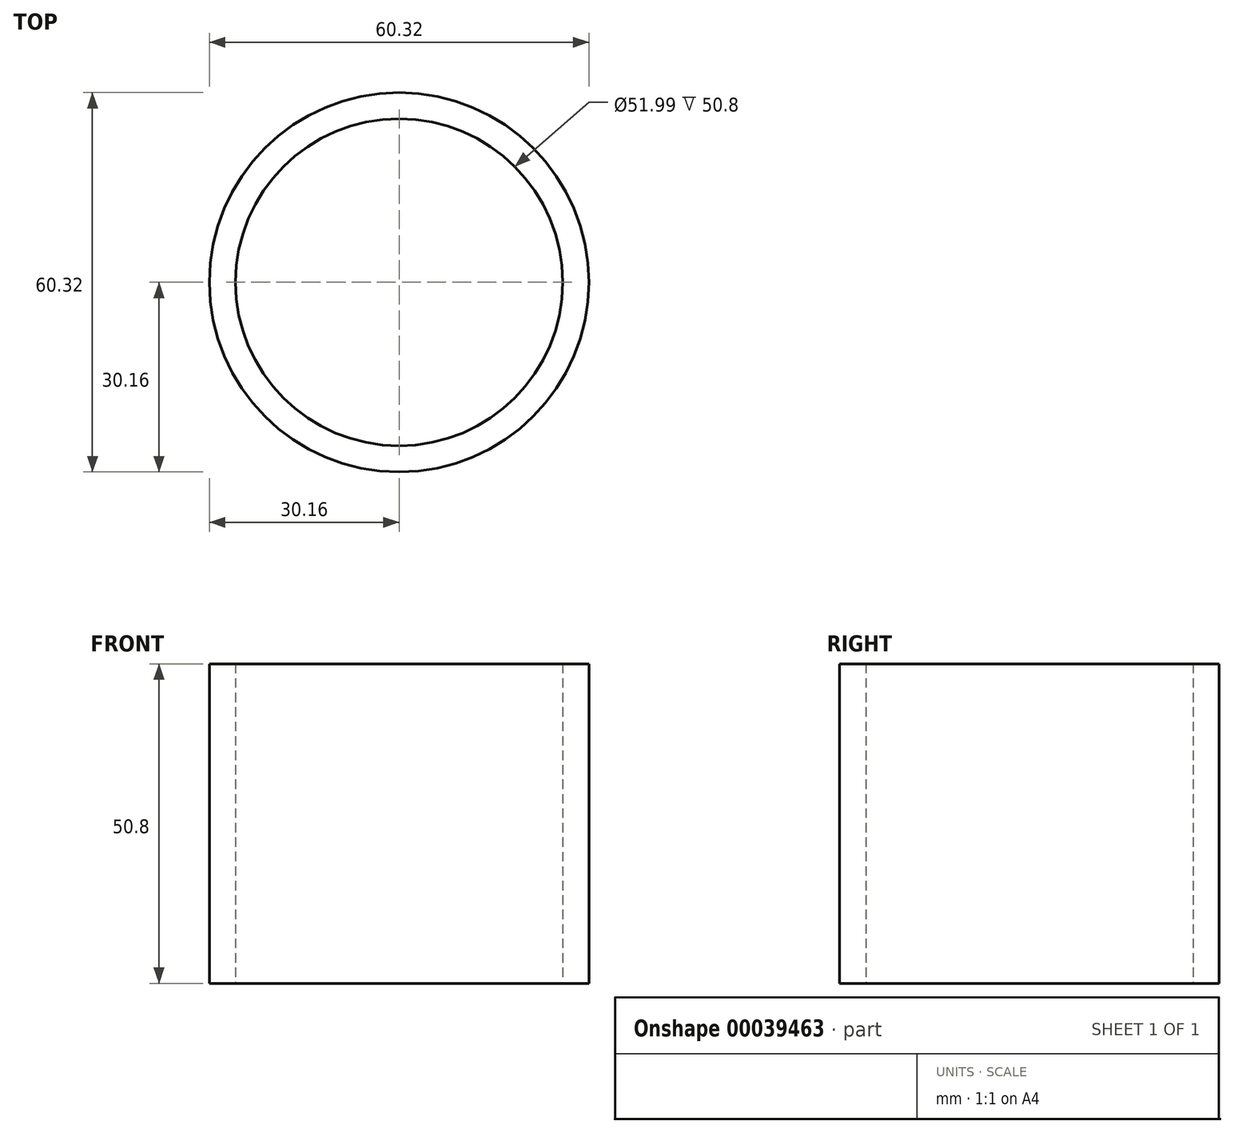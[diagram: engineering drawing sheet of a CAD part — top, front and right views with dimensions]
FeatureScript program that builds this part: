
annotation { "Feature Type Name" : "Feature", "Feature Type Description" : "" }
export const myFeature = defineFeature(function(context is Context, id is Id, definition is map)
    precondition{}
    {
        {
            var Q0;
            Q0=qCreatedBy(makeId("Top.planeOp"),FACE);
            var sketch = newSketch(context, id + "F0", { "sketchPlane" : qUnion([Q0])});
            skCircle(sketch, "E0", {"center": v(0, 0) * mm, "radius": 30.16 * mm});
            skCircle(sketch, "E1", {"center": v(0, 0) * mm, "radius": 26 * mm});
            skSolve(sketch);
        }
        {
            var Q0;
            Q0=makeQuery(id+"F0.imprint","IMPRINT",FACE,{"disambiguationData":[TD([[makeQuery(id+"F0.imprint","IMPRINT",EDGE,{"derivedFrom":sQuery(id+"F0.wireOp",EDGE,"E0")}),1.0]])]});
            extrude(context, id + "F1", {"entities" : qUnion([Q0]), "depth" : 50.8 * mm});
        }
    });
